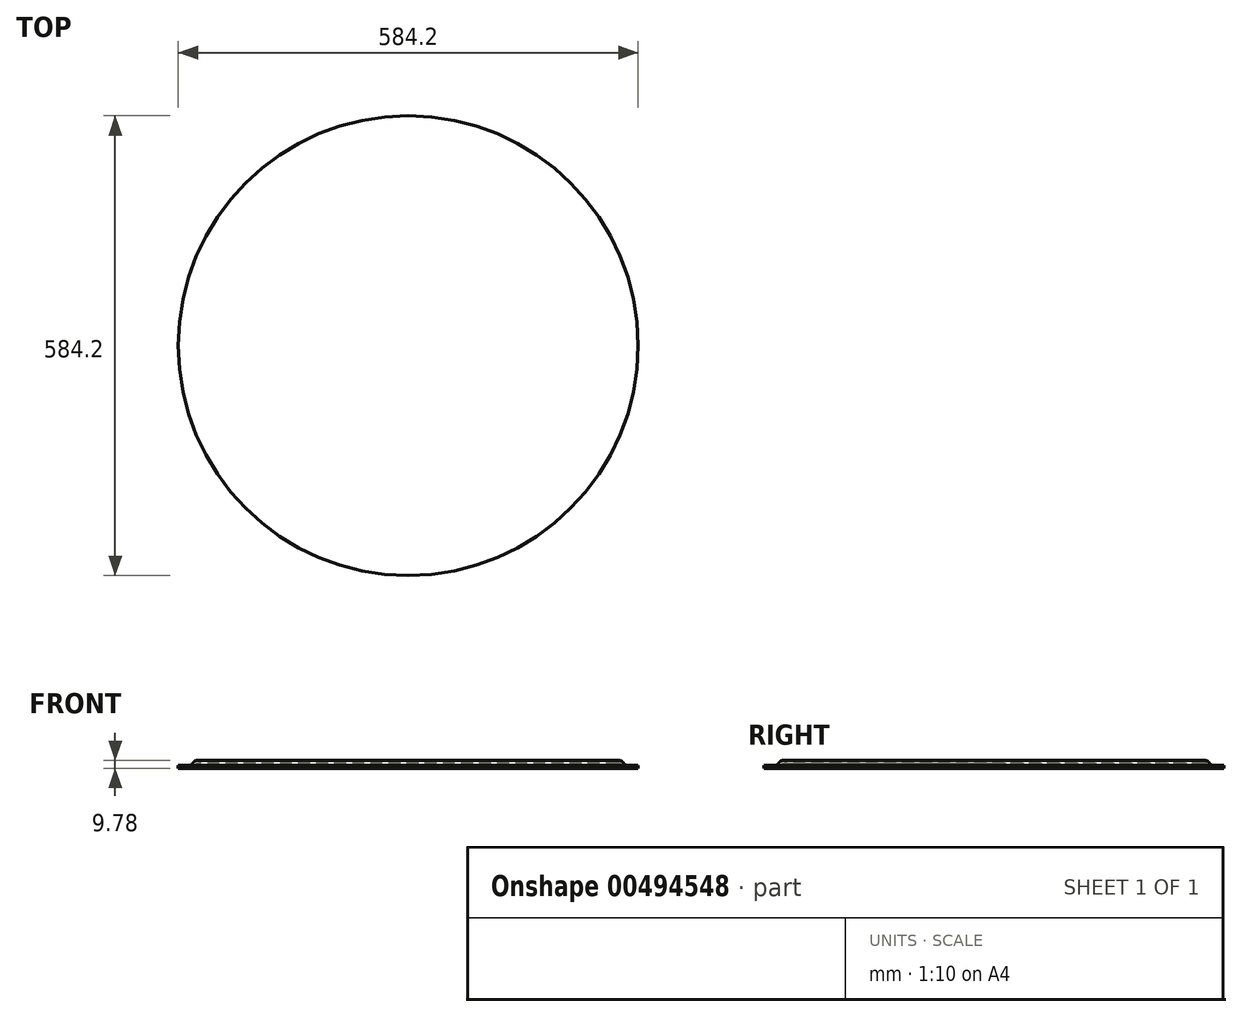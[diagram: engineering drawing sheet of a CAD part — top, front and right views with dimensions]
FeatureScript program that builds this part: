
annotation { "Feature Type Name" : "Feature", "Feature Type Description" : "" }
export const myFeature = defineFeature(function(context is Context, id is Id, definition is map)
    precondition{}
    {
        {
            var Q0;
            Q0=qCreatedBy(makeId("Front.planeOp"),FACE);
            var sketch = newSketch(context, id + "F0", { "sketchPlane" : qUnion([Q0])});
            skLineSegment(sketch, "E0", {"start": v(0, 0) * mm, "end": v(267.96, 0) * mm});
            skLineSegment(sketch, "E1", {"start": v(278.96, -6.35) * mm, "end": v(292.1, -6.35) * mm});
            skLineSegment(sketch, "E2", {"start": v(276.09, -6.35) * mm, "end": v(276.41, -6.35) * mm});
            skPoint(sketch, "E3.visualSharp", {"position": v(279.4, -6.35) * mm});
            skArc(sketch, "E3.filletArc", {"start": v(273.46, -3.17) * mm, "mid": v(275.79, -5.5) * mm, "end": v(278.96, -6.35) * mm});
            skArc(sketch, "E4.filletArc", {"start": v(273.46, -3.17) * mm, "mid": v(271.14, -0.85) * mm, "end": v(267.96, 0) * mm});
            skLineSegment(sketch, "E5.0", {"start": v(278.96, -9.78) * mm, "end": v(292.1, -9.78) * mm});
            skArc(sketch, "E5.1", {"start": v(271.18, -5.93) * mm, "mid": v(274.62, -8.76) * mm, "end": v(278.96, -9.78) * mm});
            skLineSegment(sketch, "E5.2", {"start": v(0, -3.43) * mm, "end": v(266.13, -3.43) * mm});
            skLineSegment(sketch, "E6", {"start": v(292.1, -9.78) * mm, "end": v(292.1, -6.35) * mm});
            skLineSegment(sketch, "E7", {"start": v(0, 0) * mm, "end": v(0, -3.43) * mm});
            skPoint(sketch, "E8.visualSharp", {"position": v(269.8, -3.43) * mm});
            skArc(sketch, "E8.filletArc", {"start": v(271.18, -5.93) * mm, "mid": v(268.95, -4.09) * mm, "end": v(266.13, -3.43) * mm});
            skSolve(sketch);
        }
        {
            var Q0;
            Q0 = qSketchRegion(id + "F0", true);
            var Q1;
            Q1=sQuery(id+"F0.wireOp",EDGE,"E7");
            revolve(context, id + "F1", {"entities" : qUnion([Q0]), "axis" : qUnion([Q1]), "revolveType" : RevolveType.FULL});
        }
    });
